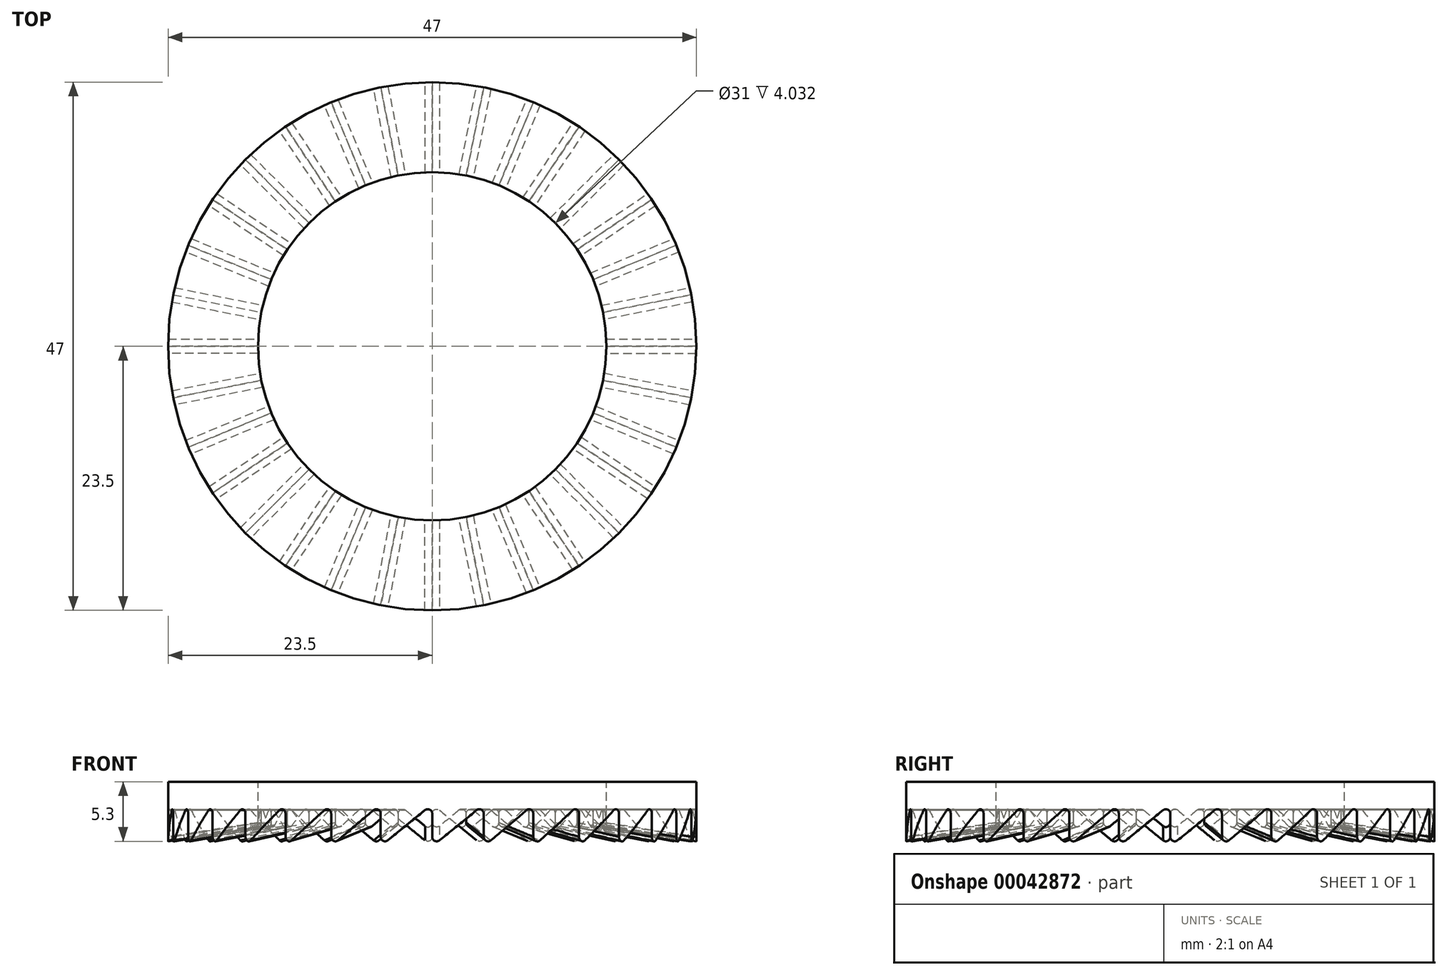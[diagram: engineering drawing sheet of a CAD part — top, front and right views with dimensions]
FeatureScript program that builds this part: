
annotation { "Feature Type Name" : "Feature", "Feature Type Description" : "" }
export const myFeature = defineFeature(function(context is Context, id is Id, definition is map)
    precondition{}
    {
        {
            var Q0;
            Q0=qCreatedBy(makeId("Top.planeOp"),FACE);
            var sketch = newSketch(context, id + "F0", { "sketchPlane" : qUnion([Q0])});
            skCircle(sketch, "E0", {"center": v(0, 0) * mm, "radius": 24 * mm});
            skCircle(sketch, "E1", {"center": v(0, 0) * mm, "radius": 25 * mm});
            skCircle(sketch, "E2", {"center": v(0, 0) * mm, "radius": 13 * mm});
            skCircle(sketch, "E3", {"center": v(0, 0) * mm, "radius": 15.5 * mm});
            skCircle(sketch, "E4", {"center": v(0, 0) * mm, "radius": 23.5 * mm});
            skCircle(sketch, "E5", {"center": v(0, 0) * mm, "radius": 12.5 * mm});
            skSolve(sketch);
        }
        {
            var Q0;
            Q0=makeQuery(id+"F0.imprint","IMPRINT",FACE,{"disambiguationData":[TD([[makeQuery(id+"F0.imprint","IMPRINT",EDGE,{"derivedFrom":sQuery(id+"F0.wireOp",EDGE,"E3")}),-1.0]])]});
            extrude(context, id + "F1", {"entities" : qUnion([Q0]), "depth" : 10 * mm});
        }
        {
            var Q0;
            Q0=qCreatedBy(makeId("Right.planeOp"),FACE);
            var sketch = newSketch(context, id + "F2", { "sketchPlane" : qUnion([Q0])});
            skLineSegment(sketch, "E6", {"start": v(0, 10) * mm, "end": v(0, 2) * mm});
            skLineSegment(sketch, "E7", {"start": v(0, 2) * mm, "end": v(9.8, 10) * mm});
            skLineSegment(sketch, "E8", {"start": v(0, 10) * mm, "end": v(9.8, 10) * mm});
            skLineSegment(sketch, "E9", {"start": v(0, 0) * mm, "end": v(12.3, 0) * mm, "construction": true});
            skLineSegment(sketch, "E10", {"start": v(6.15, 0) * mm, "end": v(0, 0) * mm, "construction": true});
            skLineSegment(sketch, "E11", {"start": v(0, 0) * mm, "end": v(-11.8, 0) * mm, "construction": true});
            skPoint(sketch, "E11.endSnap0", {"position": v(3.08, 0) * mm});
            skSolve(sketch);
        }
        {
            var Q0;
            Q0=makeQuery(id+"F2.imprint","IMPRINT",FACE,{"disambiguationData":[TD([[makeQuery(id+"F2.imprint","IMPRINT",EDGE,{"derivedFrom":sQuery(id+"F2.wireOp",EDGE,"E6")}),1.0]])]});
            extrude(context, id + "F3", {"entities" : qUnion([Q0]), "depth" : 23.5 * mm});
        }
        {
            var Q0;
            Q0=makeQuery(id+"F3.opExtrude","SWEPT_BODY",BODY,{"disambiguationData":[OSD([sQuery(id+"F2.wireOp",EDGE,"E6"),sQuery(id+"F2.wireOp",EDGE,"E7"),sQuery(id+"F2.wireOp",EDGE,"E8")])]});
            var Q1;
            Q1=makeQuery(id+"F3.opExtrude","CAP_EDGE",EDGE,{"disambiguationData":[OSD([sQuery(id+"F2.wireOp",EDGE,"E6")])],"isStart":true});
            circularPattern(context, id + "F4", {"entities" : qUnion([Q0]), "axis" : qUnion([Q1]), "angle" : 11.25 * degree, "instanceCount" : round(32)});
        }
        {
            var Q0;
            Q0=makeQuery(id+"F3.opExtrude","SWEPT_BODY",BODY,{"disambiguationData":[OSD([sQuery(id+"F2.wireOp",EDGE,"E6"),sQuery(id+"F2.wireOp",EDGE,"E7"),sQuery(id+"F2.wireOp",EDGE,"E8")])]});
            var Q1;
            Q1=makeQuery(id+"F4.opPattern","COPY",BODY,{"derivedFrom":makeQuery(id+"F3.opExtrude","SWEPT_BODY",BODY,{"disambiguationData":[OSD([sQuery(id+"F2.wireOp",EDGE,"E6"),sQuery(id+"F2.wireOp",EDGE,"E7"),sQuery(id+"F2.wireOp",EDGE,"E8")])]}),"instanceName":"1"});
            var Q2;
            Q2=makeQuery(id+"F4.opPattern","COPY",BODY,{"derivedFrom":makeQuery(id+"F3.opExtrude","SWEPT_BODY",BODY,{"disambiguationData":[OSD([sQuery(id+"F2.wireOp",EDGE,"E6"),sQuery(id+"F2.wireOp",EDGE,"E7"),sQuery(id+"F2.wireOp",EDGE,"E8")])]}),"instanceName":"2"});
            var Q3;
            Q3=makeQuery(id+"F4.opPattern","COPY",BODY,{"derivedFrom":makeQuery(id+"F3.opExtrude","SWEPT_BODY",BODY,{"disambiguationData":[OSD([sQuery(id+"F2.wireOp",EDGE,"E6"),sQuery(id+"F2.wireOp",EDGE,"E7"),sQuery(id+"F2.wireOp",EDGE,"E8")])]}),"instanceName":"3"});
            var Q4;
            Q4=makeQuery(id+"F4.opPattern","COPY",BODY,{"derivedFrom":makeQuery(id+"F3.opExtrude","SWEPT_BODY",BODY,{"disambiguationData":[OSD([sQuery(id+"F2.wireOp",EDGE,"E6"),sQuery(id+"F2.wireOp",EDGE,"E7"),sQuery(id+"F2.wireOp",EDGE,"E8")])]}),"instanceName":"4"});
            var Q5;
            Q5=makeQuery(id+"F4.opPattern","COPY",BODY,{"derivedFrom":makeQuery(id+"F3.opExtrude","SWEPT_BODY",BODY,{"disambiguationData":[OSD([sQuery(id+"F2.wireOp",EDGE,"E6"),sQuery(id+"F2.wireOp",EDGE,"E7"),sQuery(id+"F2.wireOp",EDGE,"E8")])]}),"instanceName":"5"});
            var Q6;
            Q6=makeQuery(id+"F4.opPattern","COPY",BODY,{"derivedFrom":makeQuery(id+"F3.opExtrude","SWEPT_BODY",BODY,{"disambiguationData":[OSD([sQuery(id+"F2.wireOp",EDGE,"E6"),sQuery(id+"F2.wireOp",EDGE,"E7"),sQuery(id+"F2.wireOp",EDGE,"E8")])]}),"instanceName":"6"});
            var Q7;
            Q7=makeQuery(id+"F4.opPattern","COPY",BODY,{"derivedFrom":makeQuery(id+"F3.opExtrude","SWEPT_BODY",BODY,{"disambiguationData":[OSD([sQuery(id+"F2.wireOp",EDGE,"E6"),sQuery(id+"F2.wireOp",EDGE,"E7"),sQuery(id+"F2.wireOp",EDGE,"E8")])]}),"instanceName":"7"});
            var Q8;
            Q8=makeQuery(id+"F4.opPattern","COPY",BODY,{"derivedFrom":makeQuery(id+"F3.opExtrude","SWEPT_BODY",BODY,{"disambiguationData":[OSD([sQuery(id+"F2.wireOp",EDGE,"E6"),sQuery(id+"F2.wireOp",EDGE,"E7"),sQuery(id+"F2.wireOp",EDGE,"E8")])]}),"instanceName":"8"});
            var Q9;
            Q9=makeQuery(id+"F4.opPattern","COPY",BODY,{"derivedFrom":makeQuery(id+"F3.opExtrude","SWEPT_BODY",BODY,{"disambiguationData":[OSD([sQuery(id+"F2.wireOp",EDGE,"E6"),sQuery(id+"F2.wireOp",EDGE,"E7"),sQuery(id+"F2.wireOp",EDGE,"E8")])]}),"instanceName":"9"});
            var Q10;
            Q10=makeQuery(id+"F4.opPattern","COPY",BODY,{"derivedFrom":makeQuery(id+"F3.opExtrude","SWEPT_BODY",BODY,{"disambiguationData":[OSD([sQuery(id+"F2.wireOp",EDGE,"E6"),sQuery(id+"F2.wireOp",EDGE,"E7"),sQuery(id+"F2.wireOp",EDGE,"E8")])]}),"instanceName":"10"});
            var Q11;
            Q11=makeQuery(id+"F4.opPattern","COPY",BODY,{"derivedFrom":makeQuery(id+"F3.opExtrude","SWEPT_BODY",BODY,{"disambiguationData":[OSD([sQuery(id+"F2.wireOp",EDGE,"E6"),sQuery(id+"F2.wireOp",EDGE,"E7"),sQuery(id+"F2.wireOp",EDGE,"E8")])]}),"instanceName":"11"});
            var Q12;
            Q12=makeQuery(id+"F4.opPattern","COPY",BODY,{"derivedFrom":makeQuery(id+"F3.opExtrude","SWEPT_BODY",BODY,{"disambiguationData":[OSD([sQuery(id+"F2.wireOp",EDGE,"E6"),sQuery(id+"F2.wireOp",EDGE,"E7"),sQuery(id+"F2.wireOp",EDGE,"E8")])]}),"instanceName":"12"});
            var Q13;
            Q13=makeQuery(id+"F4.opPattern","COPY",BODY,{"derivedFrom":makeQuery(id+"F3.opExtrude","SWEPT_BODY",BODY,{"disambiguationData":[OSD([sQuery(id+"F2.wireOp",EDGE,"E6"),sQuery(id+"F2.wireOp",EDGE,"E7"),sQuery(id+"F2.wireOp",EDGE,"E8")])]}),"instanceName":"13"});
            var Q14;
            Q14=makeQuery(id+"F4.opPattern","COPY",BODY,{"derivedFrom":makeQuery(id+"F3.opExtrude","SWEPT_BODY",BODY,{"disambiguationData":[OSD([sQuery(id+"F2.wireOp",EDGE,"E6"),sQuery(id+"F2.wireOp",EDGE,"E7"),sQuery(id+"F2.wireOp",EDGE,"E8")])]}),"instanceName":"14"});
            var Q15;
            Q15=makeQuery(id+"F4.opPattern","COPY",BODY,{"derivedFrom":makeQuery(id+"F3.opExtrude","SWEPT_BODY",BODY,{"disambiguationData":[OSD([sQuery(id+"F2.wireOp",EDGE,"E6"),sQuery(id+"F2.wireOp",EDGE,"E7"),sQuery(id+"F2.wireOp",EDGE,"E8")])]}),"instanceName":"15"});
            var Q16;
            Q16=makeQuery(id+"F4.opPattern","COPY",BODY,{"derivedFrom":makeQuery(id+"F3.opExtrude","SWEPT_BODY",BODY,{"disambiguationData":[OSD([sQuery(id+"F2.wireOp",EDGE,"E6"),sQuery(id+"F2.wireOp",EDGE,"E7"),sQuery(id+"F2.wireOp",EDGE,"E8")])]}),"instanceName":"16"});
            var Q17;
            Q17=makeQuery(id+"F4.opPattern","COPY",BODY,{"derivedFrom":makeQuery(id+"F3.opExtrude","SWEPT_BODY",BODY,{"disambiguationData":[OSD([sQuery(id+"F2.wireOp",EDGE,"E6"),sQuery(id+"F2.wireOp",EDGE,"E7"),sQuery(id+"F2.wireOp",EDGE,"E8")])]}),"instanceName":"17"});
            var Q18;
            Q18=makeQuery(id+"F4.opPattern","COPY",BODY,{"derivedFrom":makeQuery(id+"F3.opExtrude","SWEPT_BODY",BODY,{"disambiguationData":[OSD([sQuery(id+"F2.wireOp",EDGE,"E6"),sQuery(id+"F2.wireOp",EDGE,"E7"),sQuery(id+"F2.wireOp",EDGE,"E8")])]}),"instanceName":"18"});
            var Q19;
            Q19=makeQuery(id+"F4.opPattern","COPY",BODY,{"derivedFrom":makeQuery(id+"F3.opExtrude","SWEPT_BODY",BODY,{"disambiguationData":[OSD([sQuery(id+"F2.wireOp",EDGE,"E6"),sQuery(id+"F2.wireOp",EDGE,"E7"),sQuery(id+"F2.wireOp",EDGE,"E8")])]}),"instanceName":"19"});
            var Q20;
            Q20=makeQuery(id+"F4.opPattern","COPY",BODY,{"derivedFrom":makeQuery(id+"F3.opExtrude","SWEPT_BODY",BODY,{"disambiguationData":[OSD([sQuery(id+"F2.wireOp",EDGE,"E6"),sQuery(id+"F2.wireOp",EDGE,"E7"),sQuery(id+"F2.wireOp",EDGE,"E8")])]}),"instanceName":"20"});
            var Q21;
            Q21=makeQuery(id+"F4.opPattern","COPY",BODY,{"derivedFrom":makeQuery(id+"F3.opExtrude","SWEPT_BODY",BODY,{"disambiguationData":[OSD([sQuery(id+"F2.wireOp",EDGE,"E6"),sQuery(id+"F2.wireOp",EDGE,"E7"),sQuery(id+"F2.wireOp",EDGE,"E8")])]}),"instanceName":"21"});
            var Q22;
            Q22=makeQuery(id+"F4.opPattern","COPY",BODY,{"derivedFrom":makeQuery(id+"F3.opExtrude","SWEPT_BODY",BODY,{"disambiguationData":[OSD([sQuery(id+"F2.wireOp",EDGE,"E6"),sQuery(id+"F2.wireOp",EDGE,"E7"),sQuery(id+"F2.wireOp",EDGE,"E8")])]}),"instanceName":"22"});
            var Q23;
            Q23=makeQuery(id+"F4.opPattern","COPY",BODY,{"derivedFrom":makeQuery(id+"F3.opExtrude","SWEPT_BODY",BODY,{"disambiguationData":[OSD([sQuery(id+"F2.wireOp",EDGE,"E6"),sQuery(id+"F2.wireOp",EDGE,"E7"),sQuery(id+"F2.wireOp",EDGE,"E8")])]}),"instanceName":"23"});
            var Q24;
            Q24=makeQuery(id+"F4.opPattern","COPY",BODY,{"derivedFrom":makeQuery(id+"F3.opExtrude","SWEPT_BODY",BODY,{"disambiguationData":[OSD([sQuery(id+"F2.wireOp",EDGE,"E6"),sQuery(id+"F2.wireOp",EDGE,"E7"),sQuery(id+"F2.wireOp",EDGE,"E8")])]}),"instanceName":"24"});
            var Q25;
            Q25=makeQuery(id+"F4.opPattern","COPY",BODY,{"derivedFrom":makeQuery(id+"F3.opExtrude","SWEPT_BODY",BODY,{"disambiguationData":[OSD([sQuery(id+"F2.wireOp",EDGE,"E6"),sQuery(id+"F2.wireOp",EDGE,"E7"),sQuery(id+"F2.wireOp",EDGE,"E8")])]}),"instanceName":"25"});
            var Q26;
            Q26=makeQuery(id+"F4.opPattern","COPY",BODY,{"derivedFrom":makeQuery(id+"F3.opExtrude","SWEPT_BODY",BODY,{"disambiguationData":[OSD([sQuery(id+"F2.wireOp",EDGE,"E6"),sQuery(id+"F2.wireOp",EDGE,"E7"),sQuery(id+"F2.wireOp",EDGE,"E8")])]}),"instanceName":"26"});
            var Q27;
            Q27=makeQuery(id+"F4.opPattern","COPY",BODY,{"derivedFrom":makeQuery(id+"F3.opExtrude","SWEPT_BODY",BODY,{"disambiguationData":[OSD([sQuery(id+"F2.wireOp",EDGE,"E6"),sQuery(id+"F2.wireOp",EDGE,"E7"),sQuery(id+"F2.wireOp",EDGE,"E8")])]}),"instanceName":"27"});
            var Q28;
            Q28=makeQuery(id+"F4.opPattern","COPY",BODY,{"derivedFrom":makeQuery(id+"F3.opExtrude","SWEPT_BODY",BODY,{"disambiguationData":[OSD([sQuery(id+"F2.wireOp",EDGE,"E6"),sQuery(id+"F2.wireOp",EDGE,"E7"),sQuery(id+"F2.wireOp",EDGE,"E8")])]}),"instanceName":"28"});
            var Q29;
            Q29=makeQuery(id+"F4.opPattern","COPY",BODY,{"derivedFrom":makeQuery(id+"F3.opExtrude","SWEPT_BODY",BODY,{"disambiguationData":[OSD([sQuery(id+"F2.wireOp",EDGE,"E6"),sQuery(id+"F2.wireOp",EDGE,"E7"),sQuery(id+"F2.wireOp",EDGE,"E8")])]}),"instanceName":"29"});
            var Q30;
            Q30=makeQuery(id+"F4.opPattern","COPY",BODY,{"derivedFrom":makeQuery(id+"F3.opExtrude","SWEPT_BODY",BODY,{"disambiguationData":[OSD([sQuery(id+"F2.wireOp",EDGE,"E6"),sQuery(id+"F2.wireOp",EDGE,"E7"),sQuery(id+"F2.wireOp",EDGE,"E8")])]}),"instanceName":"30"});
            var Q31;
            Q31=makeQuery(id+"F4.opPattern","COPY",BODY,{"derivedFrom":makeQuery(id+"F3.opExtrude","SWEPT_BODY",BODY,{"disambiguationData":[OSD([sQuery(id+"F2.wireOp",EDGE,"E6"),sQuery(id+"F2.wireOp",EDGE,"E7"),sQuery(id+"F2.wireOp",EDGE,"E8")])]}),"instanceName":"31"});
            booleanBodies(context, id + "F5", {"operationType" : BooleanOperationType.UNION, "tools" : qUnion([Q0, Q1, Q2, Q3, Q4, Q5, Q6, Q7, Q8, Q9, Q10, Q11, Q12, Q13, Q14, Q15, Q16, Q17, Q18, Q19, Q20, Q21, Q22, Q23, Q24, Q25, Q26, Q27, Q28, Q29, Q30, Q31])});
        }
        {
            var Q0;
            Q0=makeQuery(id+"F3.opExtrude","SWEPT_BODY",BODY,{"disambiguationData":[OSD([sQuery(id+"F2.wireOp",EDGE,"E6"),sQuery(id+"F2.wireOp",EDGE,"E7"),sQuery(id+"F2.wireOp",EDGE,"E8")])]});
            var Q1;
            Q1=makeQuery(id+"F1.opExtrude","SWEPT_BODY",BODY,{"disambiguationData":[OSD([sQuery(id+"F0.wireOp",EDGE,"E3"),sQuery(id+"F0.wireOp",EDGE,"E4")])]});
            booleanBodies(context, id + "F6", {"operationType" : BooleanOperationType.SUBTRACTION, "tools" : qUnion([Q0]), "targets" : qUnion([Q1])});
        }
        {
            var Q0;
            Q0=makeQuery(id+"F6.opBoolean","COPY",EDGE,{"derivedFrom":makeQuery(id+"F4.opPattern","COPY",EDGE,{"derivedFrom":makeQuery(id+"F3.opExtrude","SWEPT_EDGE",EDGE,{"disambiguationData":[OSD([sQuery(id+"F2.wireOp",EDGE,"E6"),sQuery(id+"F2.wireOp",EDGE,"E7")])]}),"instanceName":"6"})});
            var Q1;
            Q1=makeQuery(id+"F6.opBoolean","COPY",EDGE,{"derivedFrom":makeQuery(id+"F5.opBoolean","INTERSECT",EDGE,{"derivedFrom":[makeQuery(id+"F4.opPattern","COPY",FACE,{"derivedFrom":makeQuery(id+"F3.opExtrude","SWEPT_FACE",FACE,{"disambiguationData":[OSD([sQuery(id+"F2.wireOp",EDGE,"E6")])]}),"instanceName":"5"}),makeQuery(id+"F4.opPattern","COPY",FACE,{"derivedFrom":makeQuery(id+"F3.opExtrude","SWEPT_FACE",FACE,{"disambiguationData":[OSD([sQuery(id+"F2.wireOp",EDGE,"E7")])]}),"instanceName":"6"})]})});
            var Q2;
            Q2=makeQuery(id+"F6.opBoolean","COPY",EDGE,{"derivedFrom":makeQuery(id+"F4.opPattern","COPY",EDGE,{"derivedFrom":makeQuery(id+"F3.opExtrude","SWEPT_EDGE",EDGE,{"disambiguationData":[OSD([sQuery(id+"F2.wireOp",EDGE,"E6"),sQuery(id+"F2.wireOp",EDGE,"E7")])]}),"instanceName":"5"})});
            var Q3;
            Q3=makeQuery(id+"F6.opBoolean","COPY",EDGE,{"derivedFrom":makeQuery(id+"F5.opBoolean","INTERSECT",EDGE,{"derivedFrom":[makeQuery(id+"F4.opPattern","COPY",FACE,{"derivedFrom":makeQuery(id+"F3.opExtrude","SWEPT_FACE",FACE,{"disambiguationData":[OSD([sQuery(id+"F2.wireOp",EDGE,"E6")])]}),"instanceName":"4"}),makeQuery(id+"F4.opPattern","COPY",FACE,{"derivedFrom":makeQuery(id+"F3.opExtrude","SWEPT_FACE",FACE,{"disambiguationData":[OSD([sQuery(id+"F2.wireOp",EDGE,"E7")])]}),"instanceName":"5"})]})});
            var Q4;
            Q4=makeQuery(id+"F6.opBoolean","COPY",EDGE,{"derivedFrom":makeQuery(id+"F4.opPattern","COPY",EDGE,{"derivedFrom":makeQuery(id+"F3.opExtrude","SWEPT_EDGE",EDGE,{"disambiguationData":[OSD([sQuery(id+"F2.wireOp",EDGE,"E6"),sQuery(id+"F2.wireOp",EDGE,"E7")])]}),"instanceName":"4"})});
            var Q5;
            Q5=makeQuery(id+"F6.opBoolean","COPY",EDGE,{"derivedFrom":makeQuery(id+"F5.opBoolean","INTERSECT",EDGE,{"derivedFrom":[makeQuery(id+"F4.opPattern","COPY",FACE,{"derivedFrom":makeQuery(id+"F3.opExtrude","SWEPT_FACE",FACE,{"disambiguationData":[OSD([sQuery(id+"F2.wireOp",EDGE,"E6")])]}),"instanceName":"3"}),makeQuery(id+"F4.opPattern","COPY",FACE,{"derivedFrom":makeQuery(id+"F3.opExtrude","SWEPT_FACE",FACE,{"disambiguationData":[OSD([sQuery(id+"F2.wireOp",EDGE,"E7")])]}),"instanceName":"4"})]})});
            var Q6;
            Q6=makeQuery(id+"F6.opBoolean","COPY",EDGE,{"derivedFrom":makeQuery(id+"F4.opPattern","COPY",EDGE,{"derivedFrom":makeQuery(id+"F3.opExtrude","SWEPT_EDGE",EDGE,{"disambiguationData":[OSD([sQuery(id+"F2.wireOp",EDGE,"E6"),sQuery(id+"F2.wireOp",EDGE,"E7")])]}),"instanceName":"3"})});
            var Q7;
            Q7=makeQuery(id+"F6.opBoolean","COPY",EDGE,{"derivedFrom":makeQuery(id+"F5.opBoolean","INTERSECT",EDGE,{"derivedFrom":[makeQuery(id+"F4.opPattern","COPY",FACE,{"derivedFrom":makeQuery(id+"F3.opExtrude","SWEPT_FACE",FACE,{"disambiguationData":[OSD([sQuery(id+"F2.wireOp",EDGE,"E6")])]}),"instanceName":"2"}),makeQuery(id+"F4.opPattern","COPY",FACE,{"derivedFrom":makeQuery(id+"F3.opExtrude","SWEPT_FACE",FACE,{"disambiguationData":[OSD([sQuery(id+"F2.wireOp",EDGE,"E7")])]}),"instanceName":"3"})]})});
            var Q8;
            Q8=makeQuery(id+"F6.opBoolean","COPY",EDGE,{"derivedFrom":makeQuery(id+"F4.opPattern","COPY",EDGE,{"derivedFrom":makeQuery(id+"F3.opExtrude","SWEPT_EDGE",EDGE,{"disambiguationData":[OSD([sQuery(id+"F2.wireOp",EDGE,"E6"),sQuery(id+"F2.wireOp",EDGE,"E7")])]}),"instanceName":"2"})});
            var Q9;
            Q9=makeQuery(id+"F6.opBoolean","COPY",EDGE,{"derivedFrom":makeQuery(id+"F5.opBoolean","INTERSECT",EDGE,{"derivedFrom":[makeQuery(id+"F4.opPattern","COPY",FACE,{"derivedFrom":makeQuery(id+"F3.opExtrude","SWEPT_FACE",FACE,{"disambiguationData":[OSD([sQuery(id+"F2.wireOp",EDGE,"E6")])]}),"instanceName":"1"}),makeQuery(id+"F4.opPattern","COPY",FACE,{"derivedFrom":makeQuery(id+"F3.opExtrude","SWEPT_FACE",FACE,{"disambiguationData":[OSD([sQuery(id+"F2.wireOp",EDGE,"E7")])]}),"instanceName":"2"})]})});
            var Q10;
            Q10=makeQuery(id+"F6.opBoolean","COPY",EDGE,{"derivedFrom":makeQuery(id+"F4.opPattern","COPY",EDGE,{"derivedFrom":makeQuery(id+"F3.opExtrude","SWEPT_EDGE",EDGE,{"disambiguationData":[OSD([sQuery(id+"F2.wireOp",EDGE,"E6"),sQuery(id+"F2.wireOp",EDGE,"E7")])]}),"instanceName":"1"})});
            var Q11;
            Q11=makeQuery(id+"F6.opBoolean","COPY",EDGE,{"derivedFrom":makeQuery(id+"F3.opExtrude","SWEPT_EDGE",EDGE,{"disambiguationData":[OSD([sQuery(id+"F2.wireOp",EDGE,"E6"),sQuery(id+"F2.wireOp",EDGE,"E7")])]})});
            var Q12;
            Q12=makeQuery(id+"F6.opBoolean","COPY",EDGE,{"derivedFrom":makeQuery(id+"F5.opBoolean","INTERSECT",EDGE,{"derivedFrom":[makeQuery(id+"F3.opExtrude","SWEPT_FACE",FACE,{"disambiguationData":[OSD([sQuery(id+"F2.wireOp",EDGE,"E6")])]}),makeQuery(id+"F4.opPattern","COPY",FACE,{"derivedFrom":makeQuery(id+"F3.opExtrude","SWEPT_FACE",FACE,{"disambiguationData":[OSD([sQuery(id+"F2.wireOp",EDGE,"E7")])]}),"instanceName":"1"})]})});
            var Q13;
            {var subQ0=sQuery(id+"F2.wireOp",EDGE,"E7");var subQ1=sQuery(id+"F2.wireOp",EDGE,"E6");Q13=makeQuery(id+"F6.opBoolean","COPY",EDGE,{"derivedFrom":makeQuery(id+"F5.opBoolean","INTERSECT",EDGE,{"derivedFrom":[makeQuery(id+"F3.opExtrude","SWEPT_FACE",FACE,{"disambiguationData":[OSD([subQ0])]}),makeQuery(id+"F4.opPattern","COPY",FACE,{"derivedFrom":makeQuery(id+"F3.opExtrude","CAP_FACE",FACE,{"disambiguationData":[OSD([subQ1,subQ0,sQuery(id+"F2.wireOp",EDGE,"E8")])],"isStart":true}),"instanceName":"23"}),makeQuery(id+"F4.opPattern","COPY",FACE,{"derivedFrom":makeQuery(id+"F3.opExtrude","SWEPT_FACE",FACE,{"disambiguationData":[OSD([subQ1])]}),"instanceName":"31"})]})});}
            var Q14;
            Q14=makeQuery(id+"F6.opBoolean","COPY",EDGE,{"derivedFrom":makeQuery(id+"F4.opPattern","COPY",EDGE,{"derivedFrom":makeQuery(id+"F3.opExtrude","SWEPT_EDGE",EDGE,{"disambiguationData":[OSD([sQuery(id+"F2.wireOp",EDGE,"E6"),sQuery(id+"F2.wireOp",EDGE,"E7")])]}),"instanceName":"31"})});
            var Q15;
            Q15=makeQuery(id+"F6.opBoolean","COPY",EDGE,{"derivedFrom":makeQuery(id+"F5.opBoolean","INTERSECT",EDGE,{"derivedFrom":[makeQuery(id+"F4.opPattern","COPY",FACE,{"derivedFrom":makeQuery(id+"F3.opExtrude","SWEPT_FACE",FACE,{"disambiguationData":[OSD([sQuery(id+"F2.wireOp",EDGE,"E6")])]}),"instanceName":"30"}),makeQuery(id+"F4.opPattern","COPY",FACE,{"derivedFrom":makeQuery(id+"F3.opExtrude","SWEPT_FACE",FACE,{"disambiguationData":[OSD([sQuery(id+"F2.wireOp",EDGE,"E7")])]}),"instanceName":"31"})]})});
            var Q16;
            Q16=makeQuery(id+"F6.opBoolean","COPY",EDGE,{"derivedFrom":makeQuery(id+"F5.opBoolean","INTERSECT",EDGE,{"derivedFrom":[makeQuery(id+"F4.opPattern","COPY",FACE,{"derivedFrom":makeQuery(id+"F3.opExtrude","SWEPT_FACE",FACE,{"disambiguationData":[OSD([sQuery(id+"F2.wireOp",EDGE,"E6")])]}),"instanceName":"29"}),makeQuery(id+"F4.opPattern","COPY",FACE,{"derivedFrom":makeQuery(id+"F3.opExtrude","SWEPT_FACE",FACE,{"disambiguationData":[OSD([sQuery(id+"F2.wireOp",EDGE,"E7")])]}),"instanceName":"30"})]})});
            var Q17;
            Q17=makeQuery(id+"F6.opBoolean","COPY",EDGE,{"derivedFrom":makeQuery(id+"F4.opPattern","COPY",EDGE,{"derivedFrom":makeQuery(id+"F3.opExtrude","SWEPT_EDGE",EDGE,{"disambiguationData":[OSD([sQuery(id+"F2.wireOp",EDGE,"E6"),sQuery(id+"F2.wireOp",EDGE,"E7")])]}),"instanceName":"29"})});
            var Q18;
            Q18=makeQuery(id+"F6.opBoolean","COPY",EDGE,{"derivedFrom":makeQuery(id+"F4.opPattern","COPY",EDGE,{"derivedFrom":makeQuery(id+"F3.opExtrude","SWEPT_EDGE",EDGE,{"disambiguationData":[OSD([sQuery(id+"F2.wireOp",EDGE,"E6"),sQuery(id+"F2.wireOp",EDGE,"E7")])]}),"instanceName":"30"})});
            var Q19;
            Q19=makeQuery(id+"F6.opBoolean","COPY",EDGE,{"derivedFrom":makeQuery(id+"F5.opBoolean","INTERSECT",EDGE,{"derivedFrom":[makeQuery(id+"F4.opPattern","COPY",FACE,{"derivedFrom":makeQuery(id+"F3.opExtrude","SWEPT_FACE",FACE,{"disambiguationData":[OSD([sQuery(id+"F2.wireOp",EDGE,"E6")])]}),"instanceName":"28"}),makeQuery(id+"F4.opPattern","COPY",FACE,{"derivedFrom":makeQuery(id+"F3.opExtrude","SWEPT_FACE",FACE,{"disambiguationData":[OSD([sQuery(id+"F2.wireOp",EDGE,"E7")])]}),"instanceName":"29"})]})});
            var Q20;
            Q20=makeQuery(id+"F6.opBoolean","COPY",EDGE,{"derivedFrom":makeQuery(id+"F4.opPattern","COPY",EDGE,{"derivedFrom":makeQuery(id+"F3.opExtrude","SWEPT_EDGE",EDGE,{"disambiguationData":[OSD([sQuery(id+"F2.wireOp",EDGE,"E6"),sQuery(id+"F2.wireOp",EDGE,"E7")])]}),"instanceName":"28"})});
            var Q21;
            Q21=makeQuery(id+"F6.opBoolean","COPY",EDGE,{"derivedFrom":makeQuery(id+"F5.opBoolean","INTERSECT",EDGE,{"derivedFrom":[makeQuery(id+"F4.opPattern","COPY",FACE,{"derivedFrom":makeQuery(id+"F3.opExtrude","SWEPT_FACE",FACE,{"disambiguationData":[OSD([sQuery(id+"F2.wireOp",EDGE,"E6")])]}),"instanceName":"27"}),makeQuery(id+"F4.opPattern","COPY",FACE,{"derivedFrom":makeQuery(id+"F3.opExtrude","SWEPT_FACE",FACE,{"disambiguationData":[OSD([sQuery(id+"F2.wireOp",EDGE,"E7")])]}),"instanceName":"28"})]})});
            var Q22;
            Q22=makeQuery(id+"F6.opBoolean","COPY",EDGE,{"derivedFrom":makeQuery(id+"F4.opPattern","COPY",EDGE,{"derivedFrom":makeQuery(id+"F3.opExtrude","SWEPT_EDGE",EDGE,{"disambiguationData":[OSD([sQuery(id+"F2.wireOp",EDGE,"E6"),sQuery(id+"F2.wireOp",EDGE,"E7")])]}),"instanceName":"27"})});
            var Q23;
            Q23=makeQuery(id+"F6.opBoolean","COPY",EDGE,{"derivedFrom":makeQuery(id+"F5.opBoolean","INTERSECT",EDGE,{"derivedFrom":[makeQuery(id+"F4.opPattern","COPY",FACE,{"derivedFrom":makeQuery(id+"F3.opExtrude","SWEPT_FACE",FACE,{"disambiguationData":[OSD([sQuery(id+"F2.wireOp",EDGE,"E6")])]}),"instanceName":"26"}),makeQuery(id+"F4.opPattern","COPY",FACE,{"derivedFrom":makeQuery(id+"F3.opExtrude","SWEPT_FACE",FACE,{"disambiguationData":[OSD([sQuery(id+"F2.wireOp",EDGE,"E7")])]}),"instanceName":"27"})]})});
            var Q24;
            Q24=makeQuery(id+"F6.opBoolean","COPY",EDGE,{"derivedFrom":makeQuery(id+"F4.opPattern","COPY",EDGE,{"derivedFrom":makeQuery(id+"F3.opExtrude","SWEPT_EDGE",EDGE,{"disambiguationData":[OSD([sQuery(id+"F2.wireOp",EDGE,"E6"),sQuery(id+"F2.wireOp",EDGE,"E7")])]}),"instanceName":"26"})});
            var Q25;
            Q25=makeQuery(id+"F6.opBoolean","COPY",EDGE,{"derivedFrom":makeQuery(id+"F5.opBoolean","INTERSECT",EDGE,{"derivedFrom":[makeQuery(id+"F4.opPattern","COPY",FACE,{"derivedFrom":makeQuery(id+"F3.opExtrude","SWEPT_FACE",FACE,{"disambiguationData":[OSD([sQuery(id+"F2.wireOp",EDGE,"E6")])]}),"instanceName":"25"}),makeQuery(id+"F4.opPattern","COPY",FACE,{"derivedFrom":makeQuery(id+"F3.opExtrude","SWEPT_FACE",FACE,{"disambiguationData":[OSD([sQuery(id+"F2.wireOp",EDGE,"E7")])]}),"instanceName":"26"})]})});
            var Q26;
            Q26=makeQuery(id+"F6.opBoolean","COPY",EDGE,{"derivedFrom":makeQuery(id+"F4.opPattern","COPY",EDGE,{"derivedFrom":makeQuery(id+"F3.opExtrude","SWEPT_EDGE",EDGE,{"disambiguationData":[OSD([sQuery(id+"F2.wireOp",EDGE,"E6"),sQuery(id+"F2.wireOp",EDGE,"E7")])]}),"instanceName":"25"})});
            var Q27;
            Q27=makeQuery(id+"F6.opBoolean","COPY",EDGE,{"derivedFrom":makeQuery(id+"F5.opBoolean","INTERSECT",EDGE,{"derivedFrom":[makeQuery(id+"F4.opPattern","COPY",FACE,{"derivedFrom":makeQuery(id+"F3.opExtrude","SWEPT_FACE",FACE,{"disambiguationData":[OSD([sQuery(id+"F2.wireOp",EDGE,"E6")])]}),"instanceName":"24"}),makeQuery(id+"F4.opPattern","COPY",FACE,{"derivedFrom":makeQuery(id+"F3.opExtrude","SWEPT_FACE",FACE,{"disambiguationData":[OSD([sQuery(id+"F2.wireOp",EDGE,"E7")])]}),"instanceName":"25"})]})});
            var Q28;
            Q28=makeQuery(id+"F6.opBoolean","COPY",EDGE,{"derivedFrom":makeQuery(id+"F4.opPattern","COPY",EDGE,{"derivedFrom":makeQuery(id+"F3.opExtrude","SWEPT_EDGE",EDGE,{"disambiguationData":[OSD([sQuery(id+"F2.wireOp",EDGE,"E6"),sQuery(id+"F2.wireOp",EDGE,"E7")])]}),"instanceName":"24"})});
            var Q29;
            Q29=makeQuery(id+"F6.opBoolean","COPY",EDGE,{"derivedFrom":makeQuery(id+"F5.opBoolean","INTERSECT",EDGE,{"derivedFrom":[makeQuery(id+"F4.opPattern","COPY",FACE,{"derivedFrom":makeQuery(id+"F3.opExtrude","SWEPT_FACE",FACE,{"disambiguationData":[OSD([sQuery(id+"F2.wireOp",EDGE,"E6")])]}),"instanceName":"23"}),makeQuery(id+"F4.opPattern","COPY",FACE,{"derivedFrom":makeQuery(id+"F3.opExtrude","SWEPT_FACE",FACE,{"disambiguationData":[OSD([sQuery(id+"F2.wireOp",EDGE,"E7")])]}),"instanceName":"24"})]})});
            var Q30;
            Q30=makeQuery(id+"F6.opBoolean","COPY",EDGE,{"derivedFrom":makeQuery(id+"F4.opPattern","COPY",EDGE,{"derivedFrom":makeQuery(id+"F3.opExtrude","SWEPT_EDGE",EDGE,{"disambiguationData":[OSD([sQuery(id+"F2.wireOp",EDGE,"E6"),sQuery(id+"F2.wireOp",EDGE,"E7")])]}),"instanceName":"23"})});
            var Q31;
            Q31=makeQuery(id+"F6.opBoolean","COPY",EDGE,{"derivedFrom":makeQuery(id+"F5.opBoolean","INTERSECT",EDGE,{"derivedFrom":[makeQuery(id+"F4.opPattern","COPY",FACE,{"derivedFrom":makeQuery(id+"F3.opExtrude","SWEPT_FACE",FACE,{"disambiguationData":[OSD([sQuery(id+"F2.wireOp",EDGE,"E6")])]}),"instanceName":"22"}),makeQuery(id+"F4.opPattern","COPY",FACE,{"derivedFrom":makeQuery(id+"F3.opExtrude","SWEPT_FACE",FACE,{"disambiguationData":[OSD([sQuery(id+"F2.wireOp",EDGE,"E7")])]}),"instanceName":"23"})]})});
            var Q32;
            Q32=makeQuery(id+"F6.opBoolean","COPY",EDGE,{"derivedFrom":makeQuery(id+"F4.opPattern","COPY",EDGE,{"derivedFrom":makeQuery(id+"F3.opExtrude","SWEPT_EDGE",EDGE,{"disambiguationData":[OSD([sQuery(id+"F2.wireOp",EDGE,"E6"),sQuery(id+"F2.wireOp",EDGE,"E7")])]}),"instanceName":"22"})});
            var Q33;
            Q33=makeQuery(id+"F6.opBoolean","COPY",EDGE,{"derivedFrom":makeQuery(id+"F5.opBoolean","INTERSECT",EDGE,{"derivedFrom":[makeQuery(id+"F4.opPattern","COPY",FACE,{"derivedFrom":makeQuery(id+"F3.opExtrude","SWEPT_FACE",FACE,{"disambiguationData":[OSD([sQuery(id+"F2.wireOp",EDGE,"E6")])]}),"instanceName":"21"}),makeQuery(id+"F4.opPattern","COPY",FACE,{"derivedFrom":makeQuery(id+"F3.opExtrude","SWEPT_FACE",FACE,{"disambiguationData":[OSD([sQuery(id+"F2.wireOp",EDGE,"E7")])]}),"instanceName":"22"})]})});
            var Q34;
            Q34=makeQuery(id+"F6.opBoolean","COPY",EDGE,{"derivedFrom":makeQuery(id+"F4.opPattern","COPY",EDGE,{"derivedFrom":makeQuery(id+"F3.opExtrude","SWEPT_EDGE",EDGE,{"disambiguationData":[OSD([sQuery(id+"F2.wireOp",EDGE,"E6"),sQuery(id+"F2.wireOp",EDGE,"E7")])]}),"instanceName":"21"})});
            var Q35;
            Q35=makeQuery(id+"F6.opBoolean","COPY",EDGE,{"derivedFrom":makeQuery(id+"F5.opBoolean","INTERSECT",EDGE,{"derivedFrom":[makeQuery(id+"F4.opPattern","COPY",FACE,{"derivedFrom":makeQuery(id+"F3.opExtrude","SWEPT_FACE",FACE,{"disambiguationData":[OSD([sQuery(id+"F2.wireOp",EDGE,"E6")])]}),"instanceName":"20"}),makeQuery(id+"F4.opPattern","COPY",FACE,{"derivedFrom":makeQuery(id+"F3.opExtrude","SWEPT_FACE",FACE,{"disambiguationData":[OSD([sQuery(id+"F2.wireOp",EDGE,"E7")])]}),"instanceName":"21"})]})});
            var Q36;
            Q36=makeQuery(id+"F6.opBoolean","COPY",EDGE,{"derivedFrom":makeQuery(id+"F4.opPattern","COPY",EDGE,{"derivedFrom":makeQuery(id+"F3.opExtrude","SWEPT_EDGE",EDGE,{"disambiguationData":[OSD([sQuery(id+"F2.wireOp",EDGE,"E6"),sQuery(id+"F2.wireOp",EDGE,"E7")])]}),"instanceName":"20"})});
            var Q37;
            Q37=makeQuery(id+"F6.opBoolean","COPY",EDGE,{"derivedFrom":makeQuery(id+"F5.opBoolean","INTERSECT",EDGE,{"derivedFrom":[makeQuery(id+"F4.opPattern","COPY",FACE,{"derivedFrom":makeQuery(id+"F3.opExtrude","SWEPT_FACE",FACE,{"disambiguationData":[OSD([sQuery(id+"F2.wireOp",EDGE,"E6")])]}),"instanceName":"19"}),makeQuery(id+"F4.opPattern","COPY",FACE,{"derivedFrom":makeQuery(id+"F3.opExtrude","SWEPT_FACE",FACE,{"disambiguationData":[OSD([sQuery(id+"F2.wireOp",EDGE,"E7")])]}),"instanceName":"20"})]})});
            var Q38;
            Q38=makeQuery(id+"F6.opBoolean","COPY",EDGE,{"derivedFrom":makeQuery(id+"F4.opPattern","COPY",EDGE,{"derivedFrom":makeQuery(id+"F3.opExtrude","SWEPT_EDGE",EDGE,{"disambiguationData":[OSD([sQuery(id+"F2.wireOp",EDGE,"E6"),sQuery(id+"F2.wireOp",EDGE,"E7")])]}),"instanceName":"19"})});
            var Q39;
            Q39=makeQuery(id+"F6.opBoolean","COPY",EDGE,{"derivedFrom":makeQuery(id+"F5.opBoolean","INTERSECT",EDGE,{"derivedFrom":[makeQuery(id+"F4.opPattern","COPY",FACE,{"derivedFrom":makeQuery(id+"F3.opExtrude","SWEPT_FACE",FACE,{"disambiguationData":[OSD([sQuery(id+"F2.wireOp",EDGE,"E6")])]}),"instanceName":"18"}),makeQuery(id+"F4.opPattern","COPY",FACE,{"derivedFrom":makeQuery(id+"F3.opExtrude","SWEPT_FACE",FACE,{"disambiguationData":[OSD([sQuery(id+"F2.wireOp",EDGE,"E7")])]}),"instanceName":"19"})]})});
            var Q40;
            Q40=makeQuery(id+"F6.opBoolean","COPY",EDGE,{"derivedFrom":makeQuery(id+"F4.opPattern","COPY",EDGE,{"derivedFrom":makeQuery(id+"F3.opExtrude","SWEPT_EDGE",EDGE,{"disambiguationData":[OSD([sQuery(id+"F2.wireOp",EDGE,"E6"),sQuery(id+"F2.wireOp",EDGE,"E7")])]}),"instanceName":"18"})});
            var Q41;
            Q41=makeQuery(id+"F6.opBoolean","COPY",EDGE,{"derivedFrom":makeQuery(id+"F5.opBoolean","INTERSECT",EDGE,{"derivedFrom":[makeQuery(id+"F4.opPattern","COPY",FACE,{"derivedFrom":makeQuery(id+"F3.opExtrude","SWEPT_FACE",FACE,{"disambiguationData":[OSD([sQuery(id+"F2.wireOp",EDGE,"E6")])]}),"instanceName":"17"}),makeQuery(id+"F4.opPattern","COPY",FACE,{"derivedFrom":makeQuery(id+"F3.opExtrude","SWEPT_FACE",FACE,{"disambiguationData":[OSD([sQuery(id+"F2.wireOp",EDGE,"E7")])]}),"instanceName":"18"})]})});
            var Q42;
            Q42=makeQuery(id+"F6.opBoolean","COPY",EDGE,{"derivedFrom":makeQuery(id+"F4.opPattern","COPY",EDGE,{"derivedFrom":makeQuery(id+"F3.opExtrude","SWEPT_EDGE",EDGE,{"disambiguationData":[OSD([sQuery(id+"F2.wireOp",EDGE,"E6"),sQuery(id+"F2.wireOp",EDGE,"E7")])]}),"instanceName":"17"})});
            var Q43;
            Q43=makeQuery(id+"F6.opBoolean","COPY",EDGE,{"derivedFrom":makeQuery(id+"F5.opBoolean","INTERSECT",EDGE,{"derivedFrom":[makeQuery(id+"F4.opPattern","COPY",FACE,{"derivedFrom":makeQuery(id+"F3.opExtrude","SWEPT_FACE",FACE,{"disambiguationData":[OSD([sQuery(id+"F2.wireOp",EDGE,"E6")])]}),"instanceName":"16"}),makeQuery(id+"F4.opPattern","COPY",FACE,{"derivedFrom":makeQuery(id+"F3.opExtrude","SWEPT_FACE",FACE,{"disambiguationData":[OSD([sQuery(id+"F2.wireOp",EDGE,"E7")])]}),"instanceName":"17"})]})});
            var Q44;
            Q44=makeQuery(id+"F6.opBoolean","COPY",EDGE,{"derivedFrom":makeQuery(id+"F4.opPattern","COPY",EDGE,{"derivedFrom":makeQuery(id+"F3.opExtrude","SWEPT_EDGE",EDGE,{"disambiguationData":[OSD([sQuery(id+"F2.wireOp",EDGE,"E6"),sQuery(id+"F2.wireOp",EDGE,"E7")])]}),"instanceName":"16"})});
            var Q45;
            Q45=makeQuery(id+"F6.opBoolean","COPY",EDGE,{"derivedFrom":makeQuery(id+"F5.opBoolean","INTERSECT",EDGE,{"derivedFrom":[makeQuery(id+"F4.opPattern","COPY",FACE,{"derivedFrom":makeQuery(id+"F3.opExtrude","SWEPT_FACE",FACE,{"disambiguationData":[OSD([sQuery(id+"F2.wireOp",EDGE,"E6")])]}),"instanceName":"15"}),makeQuery(id+"F4.opPattern","COPY",FACE,{"derivedFrom":makeQuery(id+"F3.opExtrude","SWEPT_FACE",FACE,{"disambiguationData":[OSD([sQuery(id+"F2.wireOp",EDGE,"E7")])]}),"instanceName":"16"})]})});
            var Q46;
            Q46=makeQuery(id+"F6.opBoolean","COPY",EDGE,{"derivedFrom":makeQuery(id+"F4.opPattern","COPY",EDGE,{"derivedFrom":makeQuery(id+"F3.opExtrude","SWEPT_EDGE",EDGE,{"disambiguationData":[OSD([sQuery(id+"F2.wireOp",EDGE,"E6"),sQuery(id+"F2.wireOp",EDGE,"E7")])]}),"instanceName":"15"})});
            var Q47;
            Q47=makeQuery(id+"F6.opBoolean","COPY",EDGE,{"derivedFrom":makeQuery(id+"F4.opPattern","COPY",EDGE,{"derivedFrom":makeQuery(id+"F3.opExtrude","SWEPT_EDGE",EDGE,{"disambiguationData":[OSD([sQuery(id+"F2.wireOp",EDGE,"E6"),sQuery(id+"F2.wireOp",EDGE,"E7")])]}),"instanceName":"14"})});
            var Q48;
            Q48=makeQuery(id+"F6.opBoolean","COPY",EDGE,{"derivedFrom":makeQuery(id+"F5.opBoolean","INTERSECT",EDGE,{"derivedFrom":[makeQuery(id+"F4.opPattern","COPY",FACE,{"derivedFrom":makeQuery(id+"F3.opExtrude","SWEPT_FACE",FACE,{"disambiguationData":[OSD([sQuery(id+"F2.wireOp",EDGE,"E6")])]}),"instanceName":"15"}),makeQuery(id+"F4.opPattern","COPY",FACE,{"derivedFrom":makeQuery(id+"F3.opExtrude","SWEPT_FACE",FACE,{"disambiguationData":[OSD([sQuery(id+"F2.wireOp",EDGE,"E7")])]}),"instanceName":"16"})]})});
            var Q49;
            Q49=makeQuery(id+"F6.opBoolean","COPY",EDGE,{"derivedFrom":makeQuery(id+"F4.opPattern","COPY",EDGE,{"derivedFrom":makeQuery(id+"F3.opExtrude","SWEPT_EDGE",EDGE,{"disambiguationData":[OSD([sQuery(id+"F2.wireOp",EDGE,"E6"),sQuery(id+"F2.wireOp",EDGE,"E7")])]}),"instanceName":"15"})});
            var Q50;
            Q50=makeQuery(id+"F6.opBoolean","COPY",EDGE,{"derivedFrom":makeQuery(id+"F5.opBoolean","INTERSECT",EDGE,{"derivedFrom":[makeQuery(id+"F4.opPattern","COPY",FACE,{"derivedFrom":makeQuery(id+"F3.opExtrude","SWEPT_FACE",FACE,{"disambiguationData":[OSD([sQuery(id+"F2.wireOp",EDGE,"E6")])]}),"instanceName":"13"}),makeQuery(id+"F4.opPattern","COPY",FACE,{"derivedFrom":makeQuery(id+"F3.opExtrude","SWEPT_FACE",FACE,{"disambiguationData":[OSD([sQuery(id+"F2.wireOp",EDGE,"E7")])]}),"instanceName":"14"})]})});
            var Q51;
            Q51=makeQuery(id+"F6.opBoolean","COPY",EDGE,{"derivedFrom":makeQuery(id+"F5.opBoolean","INTERSECT",EDGE,{"derivedFrom":[makeQuery(id+"F4.opPattern","COPY",FACE,{"derivedFrom":makeQuery(id+"F3.opExtrude","SWEPT_FACE",FACE,{"disambiguationData":[OSD([sQuery(id+"F2.wireOp",EDGE,"E6")])]}),"instanceName":"14"}),makeQuery(id+"F4.opPattern","COPY",FACE,{"derivedFrom":makeQuery(id+"F3.opExtrude","SWEPT_FACE",FACE,{"disambiguationData":[OSD([sQuery(id+"F2.wireOp",EDGE,"E7")])]}),"instanceName":"15"})]})});
            var Q52;
            Q52=makeQuery(id+"F6.opBoolean","COPY",EDGE,{"derivedFrom":makeQuery(id+"F4.opPattern","COPY",EDGE,{"derivedFrom":makeQuery(id+"F3.opExtrude","SWEPT_EDGE",EDGE,{"disambiguationData":[OSD([sQuery(id+"F2.wireOp",EDGE,"E6"),sQuery(id+"F2.wireOp",EDGE,"E7")])]}),"instanceName":"13"})});
            var Q53;
            Q53=makeQuery(id+"F6.opBoolean","COPY",EDGE,{"derivedFrom":makeQuery(id+"F5.opBoolean","INTERSECT",EDGE,{"derivedFrom":[makeQuery(id+"F4.opPattern","COPY",FACE,{"derivedFrom":makeQuery(id+"F3.opExtrude","SWEPT_FACE",FACE,{"disambiguationData":[OSD([sQuery(id+"F2.wireOp",EDGE,"E6")])]}),"instanceName":"12"}),makeQuery(id+"F4.opPattern","COPY",FACE,{"derivedFrom":makeQuery(id+"F3.opExtrude","SWEPT_FACE",FACE,{"disambiguationData":[OSD([sQuery(id+"F2.wireOp",EDGE,"E7")])]}),"instanceName":"13"})]})});
            var Q54;
            Q54=makeQuery(id+"F6.opBoolean","COPY",EDGE,{"derivedFrom":makeQuery(id+"F4.opPattern","COPY",EDGE,{"derivedFrom":makeQuery(id+"F3.opExtrude","SWEPT_EDGE",EDGE,{"disambiguationData":[OSD([sQuery(id+"F2.wireOp",EDGE,"E6"),sQuery(id+"F2.wireOp",EDGE,"E7")])]}),"instanceName":"12"})});
            var Q55;
            Q55=makeQuery(id+"F6.opBoolean","COPY",EDGE,{"derivedFrom":makeQuery(id+"F5.opBoolean","INTERSECT",EDGE,{"derivedFrom":[makeQuery(id+"F4.opPattern","COPY",FACE,{"derivedFrom":makeQuery(id+"F3.opExtrude","SWEPT_FACE",FACE,{"disambiguationData":[OSD([sQuery(id+"F2.wireOp",EDGE,"E6")])]}),"instanceName":"11"}),makeQuery(id+"F4.opPattern","COPY",FACE,{"derivedFrom":makeQuery(id+"F3.opExtrude","SWEPT_FACE",FACE,{"disambiguationData":[OSD([sQuery(id+"F2.wireOp",EDGE,"E7")])]}),"instanceName":"12"})]})});
            var Q56;
            Q56=makeQuery(id+"F6.opBoolean","COPY",EDGE,{"derivedFrom":makeQuery(id+"F4.opPattern","COPY",EDGE,{"derivedFrom":makeQuery(id+"F3.opExtrude","SWEPT_EDGE",EDGE,{"disambiguationData":[OSD([sQuery(id+"F2.wireOp",EDGE,"E6"),sQuery(id+"F2.wireOp",EDGE,"E7")])]}),"instanceName":"11"})});
            var Q57;
            Q57=makeQuery(id+"F6.opBoolean","COPY",EDGE,{"derivedFrom":makeQuery(id+"F5.opBoolean","INTERSECT",EDGE,{"derivedFrom":[makeQuery(id+"F4.opPattern","COPY",FACE,{"derivedFrom":makeQuery(id+"F3.opExtrude","SWEPT_FACE",FACE,{"disambiguationData":[OSD([sQuery(id+"F2.wireOp",EDGE,"E6")])]}),"instanceName":"10"}),makeQuery(id+"F4.opPattern","COPY",FACE,{"derivedFrom":makeQuery(id+"F3.opExtrude","SWEPT_FACE",FACE,{"disambiguationData":[OSD([sQuery(id+"F2.wireOp",EDGE,"E7")])]}),"instanceName":"11"})]})});
            var Q58;
            Q58=makeQuery(id+"F6.opBoolean","COPY",EDGE,{"derivedFrom":makeQuery(id+"F4.opPattern","COPY",EDGE,{"derivedFrom":makeQuery(id+"F3.opExtrude","SWEPT_EDGE",EDGE,{"disambiguationData":[OSD([sQuery(id+"F2.wireOp",EDGE,"E6"),sQuery(id+"F2.wireOp",EDGE,"E7")])]}),"instanceName":"10"})});
            var Q59;
            Q59=makeQuery(id+"F6.opBoolean","COPY",EDGE,{"derivedFrom":makeQuery(id+"F5.opBoolean","INTERSECT",EDGE,{"derivedFrom":[makeQuery(id+"F4.opPattern","COPY",FACE,{"derivedFrom":makeQuery(id+"F3.opExtrude","SWEPT_FACE",FACE,{"disambiguationData":[OSD([sQuery(id+"F2.wireOp",EDGE,"E6")])]}),"instanceName":"9"}),makeQuery(id+"F4.opPattern","COPY",FACE,{"derivedFrom":makeQuery(id+"F3.opExtrude","SWEPT_FACE",FACE,{"disambiguationData":[OSD([sQuery(id+"F2.wireOp",EDGE,"E7")])]}),"instanceName":"10"})]})});
            var Q60;
            Q60=makeQuery(id+"F6.opBoolean","COPY",EDGE,{"derivedFrom":makeQuery(id+"F4.opPattern","COPY",EDGE,{"derivedFrom":makeQuery(id+"F3.opExtrude","SWEPT_EDGE",EDGE,{"disambiguationData":[OSD([sQuery(id+"F2.wireOp",EDGE,"E6"),sQuery(id+"F2.wireOp",EDGE,"E7")])]}),"instanceName":"9"})});
            var Q61;
            Q61=makeQuery(id+"F6.opBoolean","COPY",EDGE,{"derivedFrom":makeQuery(id+"F5.opBoolean","INTERSECT",EDGE,{"derivedFrom":[makeQuery(id+"F4.opPattern","COPY",FACE,{"derivedFrom":makeQuery(id+"F3.opExtrude","SWEPT_FACE",FACE,{"disambiguationData":[OSD([sQuery(id+"F2.wireOp",EDGE,"E6")])]}),"instanceName":"8"}),makeQuery(id+"F4.opPattern","COPY",FACE,{"derivedFrom":makeQuery(id+"F3.opExtrude","SWEPT_FACE",FACE,{"disambiguationData":[OSD([sQuery(id+"F2.wireOp",EDGE,"E7")])]}),"instanceName":"9"})]})});
            var Q62;
            Q62=makeQuery(id+"F6.opBoolean","COPY",EDGE,{"derivedFrom":makeQuery(id+"F4.opPattern","COPY",EDGE,{"derivedFrom":makeQuery(id+"F3.opExtrude","SWEPT_EDGE",EDGE,{"disambiguationData":[OSD([sQuery(id+"F2.wireOp",EDGE,"E6"),sQuery(id+"F2.wireOp",EDGE,"E7")])]}),"instanceName":"8"})});
            var Q63;
            Q63=makeQuery(id+"F6.opBoolean","COPY",EDGE,{"derivedFrom":makeQuery(id+"F5.opBoolean","INTERSECT",EDGE,{"derivedFrom":[makeQuery(id+"F4.opPattern","COPY",FACE,{"derivedFrom":makeQuery(id+"F3.opExtrude","SWEPT_FACE",FACE,{"disambiguationData":[OSD([sQuery(id+"F2.wireOp",EDGE,"E6")])]}),"instanceName":"7"}),makeQuery(id+"F4.opPattern","COPY",FACE,{"derivedFrom":makeQuery(id+"F3.opExtrude","SWEPT_FACE",FACE,{"disambiguationData":[OSD([sQuery(id+"F2.wireOp",EDGE,"E7")])]}),"instanceName":"8"})]})});
            var Q64;
            Q64=makeQuery(id+"F6.opBoolean","COPY",EDGE,{"derivedFrom":makeQuery(id+"F4.opPattern","COPY",EDGE,{"derivedFrom":makeQuery(id+"F3.opExtrude","SWEPT_EDGE",EDGE,{"disambiguationData":[OSD([sQuery(id+"F2.wireOp",EDGE,"E6"),sQuery(id+"F2.wireOp",EDGE,"E7")])]}),"instanceName":"7"})});
            var Q65;
            Q65=makeQuery(id+"F6.opBoolean","COPY",EDGE,{"derivedFrom":makeQuery(id+"F5.opBoolean","INTERSECT",EDGE,{"derivedFrom":[makeQuery(id+"F4.opPattern","COPY",FACE,{"derivedFrom":makeQuery(id+"F3.opExtrude","SWEPT_FACE",FACE,{"disambiguationData":[OSD([sQuery(id+"F2.wireOp",EDGE,"E6")])]}),"instanceName":"6"}),makeQuery(id+"F4.opPattern","COPY",FACE,{"derivedFrom":makeQuery(id+"F3.opExtrude","SWEPT_FACE",FACE,{"disambiguationData":[OSD([sQuery(id+"F2.wireOp",EDGE,"E7")])]}),"instanceName":"7"})]})});
            fillet(context, id + "F7", {"entities" : qUnion([Q0, Q1, Q2, Q3, Q4, Q5, Q6, Q7, Q8, Q9, Q10, Q11, Q12, Q13, Q14, Q15, Q16, Q17, Q18, Q19, Q20, Q21, Q22, Q23, Q24, Q25, Q26, Q27, Q28, Q29, Q30, Q31, Q32, Q33, Q34, Q35, Q36, Q37, Q38, Q39, Q40, Q41, Q42, Q43, Q44, Q45, Q46, Q47, Q48, Q49, Q50, Q51, Q52, Q53, Q54, Q55, Q56, Q57, Q58, Q59, Q60, Q61, Q62, Q63, Q64, Q65]), "radius" : 0.4 * mm, "tangentPropagation" : true, "rho" : .3, "crossSection" : FilletCrossSection.CONIC, "allowEdgeOverflow" : false});
        }
        {
            var Q0;
            Q0=makeQuery(id+"F1.opExtrude","SWEPT_BODY",BODY,{"disambiguationData":[OSD([sQuery(id+"F0.wireOp",EDGE,"E3"),sQuery(id+"F0.wireOp",EDGE,"E4")])]});
            var Q1;
            Q1=sQuery(id+"F2.wireOp",EDGE,"E8");
            transform(context, id + "F8", {"entities" : qUnion([Q0]), "transformType" : TransformType.ROTATION, "transformAxis" : qUnion([Q1]), "angle" : 180 * degree, "makeCopy" : false});
        }
    });
